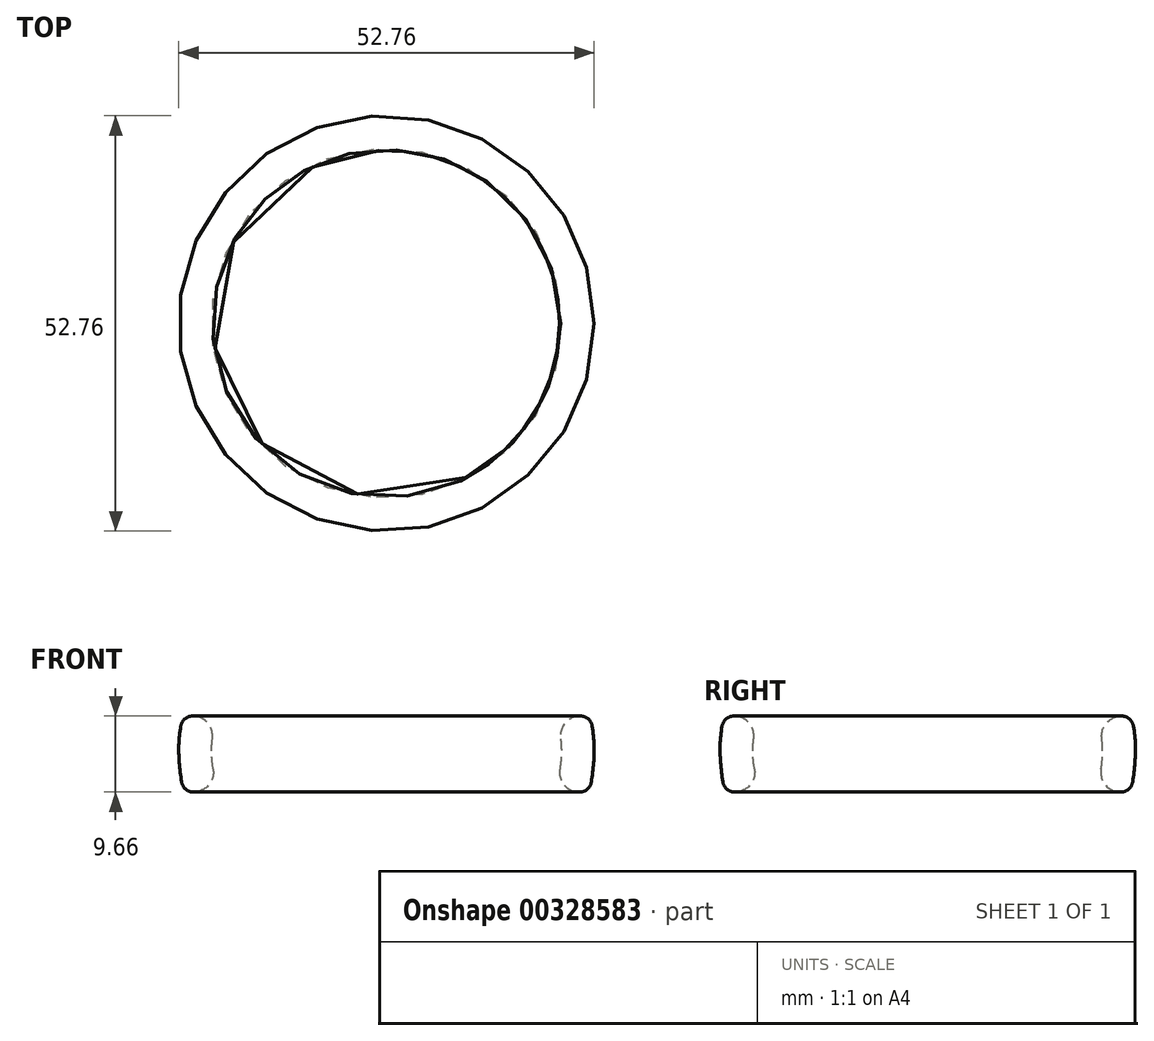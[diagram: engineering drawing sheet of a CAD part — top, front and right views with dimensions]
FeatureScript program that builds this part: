
annotation { "Feature Type Name" : "Feature", "Feature Type Description" : "" }
export const myFeature = defineFeature(function(context is Context, id is Id, definition is map)
    precondition{}
    {
        {
            var Q0;
            Q0=qCreatedBy(makeId("Front.planeOp"),FACE);
            var sketch = newSketch(context, id + "F0", { "sketchPlane" : qUnion([Q0])});
            skLineSegment(sketch, "E0", {"start": v(0, 30.25) * mm, "end": v(0, -36.67) * mm});
            skSolve(sketch);
        }
        {
            var Q0;
            Q0=qCreatedBy(makeId("Front.planeOp"),FACE);
            var sketch = newSketch(context, id + "F1", { "sketchPlane" : qUnion([Q0])});
            skLineSegment(sketch, "E1.bottom", {"start": v(24.63, 4.83) * mm, "end": v(24.63, 4.83) * mm});
            skLineSegment(sketch, "E1.top", {"start": v(24.52, -4.83) * mm, "end": v(24.52, -4.83) * mm});
            skPoint(sketch, "E1.middle", {"position": v(23.53, 0) * mm});
            skFitSpline(sketch, "E2.MirrorCS", {"points": [v(25.85, 4.83) * mm, v(25.8, -4.83) * mm], "startDerivative": vector(2.67, -10.03) * mm, "endDerivative": vector(-1.68, -9.43) * mm});
            skFitSpline(sketch, "E3", {"points": [v(21.24, 4.83) * mm, v(21.2, -4.83) * mm], "startDerivative": vector(4.46, -8.8) * mm, "endDerivative": vector(-3.36, -8.69) * mm});
            skArc(sketch, "E4.filletArc", {"start": v(24.63, 4.83) * mm, "mid": v(22.71, 3.96) * mm, "end": v(22.1, 1.95) * mm});
            skArc(sketch, "E5.filletArc", {"start": v(26.13, 3.58) * mm, "mid": v(25.6, 4.48) * mm, "end": v(24.63, 4.83) * mm});
            skArc(sketch, "E6.filletArc", {"start": v(24.52, -4.83) * mm, "mid": v(25.51, -4.47) * mm, "end": v(26.03, -3.54) * mm});
            skArc(sketch, "E7.filletArc", {"start": v(22.01, -1.87) * mm, "mid": v(22.58, -3.93) * mm, "end": v(24.52, -4.83) * mm});
            skSolve(sketch);
        }
        {
            var Q0;
            Q0=makeQuery(id+"F1.imprint","IMPRINT",FACE,{"disambiguationData":[TD([[makeQuery(id+"F1.imprint","IMPRINT",EDGE,{"derivedFrom":sQuery(id+"F1.wireOp",EDGE,"E1.bottom")}),1.0]])]});
            var Q1;
            Q1=makeQuery(id+"F1.imprint","IMPRINT",FACE,{"disambiguationData":[TD([[makeQuery(id+"F1.imprint","IMPRINT",EDGE,{"derivedFrom":sQuery(id+"F1.wireOp",EDGE,"E2.MirrorCS")}),-1.0]])]});
            var Q2;
            Q2=sQuery(id+"F0.wireOp",EDGE,"E0");
            revolve(context, id + "F2", {"entities" : qUnion([Q0, Q1]), "axis" : qUnion([Q2]), "revolveType" : RevolveType.FULL});
        }
        {
            var Q0;
            Q0=qCreatedBy(makeId("Top.planeOp"),FACE);
            var sketch = newSketch(context, id + "F3", { "sketchPlane" : qUnion([Q0])});
            skCircle(sketch, "E8", {"center": v(-0.48, -21.06) * mm, "radius": 18.76 * mm});
            skSolve(sketch);
        }
    });
